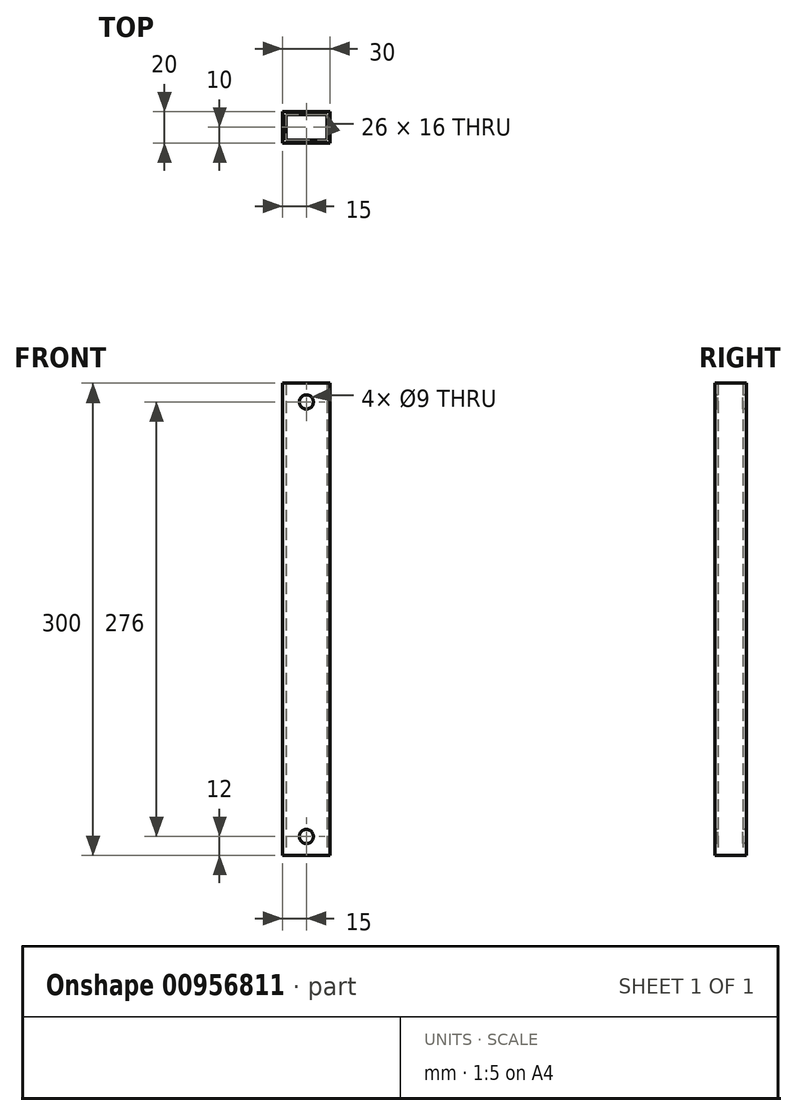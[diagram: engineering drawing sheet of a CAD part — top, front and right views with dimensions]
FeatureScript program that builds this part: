
annotation { "Feature Type Name" : "Feature", "Feature Type Description" : "" }
export const myFeature = defineFeature(function(context is Context, id is Id, definition is map)
    precondition{}
    {
        {
            var Q0;
            Q0=qCreatedBy(makeId("Top.planeOp"),FACE);
            var sketch = newSketch(context, id + "F0", { "sketchPlane" : qUnion([Q0])});
            skLineSegment(sketch, "E0.bottom", {"start": v(15, 10) * mm, "end": v(-15, 10) * mm});
            skLineSegment(sketch, "E0.top", {"start": v(15, -10) * mm, "end": v(-15, -10) * mm});
            skLineSegment(sketch, "E0.left", {"start": v(15, 10) * mm, "end": v(15, -10) * mm});
            skLineSegment(sketch, "E0.right", {"start": v(-15, 10) * mm, "end": v(-15, -10) * mm});
            skPoint(sketch, "E0.middle", {"position": v(0, 0) * mm});
            skLineSegment(sketch, "E1.bottom", {"start": v(13, 8) * mm, "end": v(-13, 8) * mm});
            skLineSegment(sketch, "E1.top", {"start": v(13, -8) * mm, "end": v(-13, -8) * mm});
            skLineSegment(sketch, "E1.left", {"start": v(13, 8) * mm, "end": v(13, -8) * mm});
            skLineSegment(sketch, "E1.right", {"start": v(-13, 8) * mm, "end": v(-13, -8) * mm});
            skSolve(sketch);
        }
        {
            var Q0;
            Q0=qSketchRegion(id+"F0",true);
            extrude(context, id + "F1", {"entities" : qUnion([Q0]), "depth" : 300 * mm, "offsetDistance" : 25 * mm});
        }
        {
            var Q0;
            Q0=makeQuery(id+"F1.opExtrude","SWEPT_FACE",FACE,{"disambiguationData":[OSD([sQuery(id+"F0.wireOp",EDGE,"E0.top")])]});
            var sketch = newSketch(context, id + "F2", { "sketchPlane" : qUnion([Q0])});
            skCircle(sketch, "E2", {"center": v(0, 288) * mm, "radius": 4.5 * mm});
            skCircle(sketch, "E3", {"center": v(0, 12) * mm, "radius": 4.5 * mm});
            skLineSegment(sketch, "E4", {"start": v(0, 288) * mm, "end": v(0, 300) * mm, "construction": true});
            skLineSegment(sketch, "E5", {"start": v(0, 12) * mm, "end": v(0, 0) * mm, "construction": true});
            skSolve(sketch);
        }
        {
            var Q0;
            Q0=qSketchRegion(id+"F2",true);
            var Q1;
            Q1=makeQuery(id+"F1.opExtrude","SWEPT_FACE",FACE,{"disambiguationData":[OSD([sQuery(id+"F0.wireOp",EDGE,"E0.bottom")])]});
            extrude(context, id + "F3", {"entities" : qUnion([Q0]), "operationType" : NewBodyOperationType.REMOVE, "endBound" : BoundingType.UP_TO_SURFACE, "oppositeDirection" : true, "depth" : 25 * mm, "endBoundEntityFace" : qUnion([Q1]), "offsetDistance" : 25 * mm});
        }
    });
